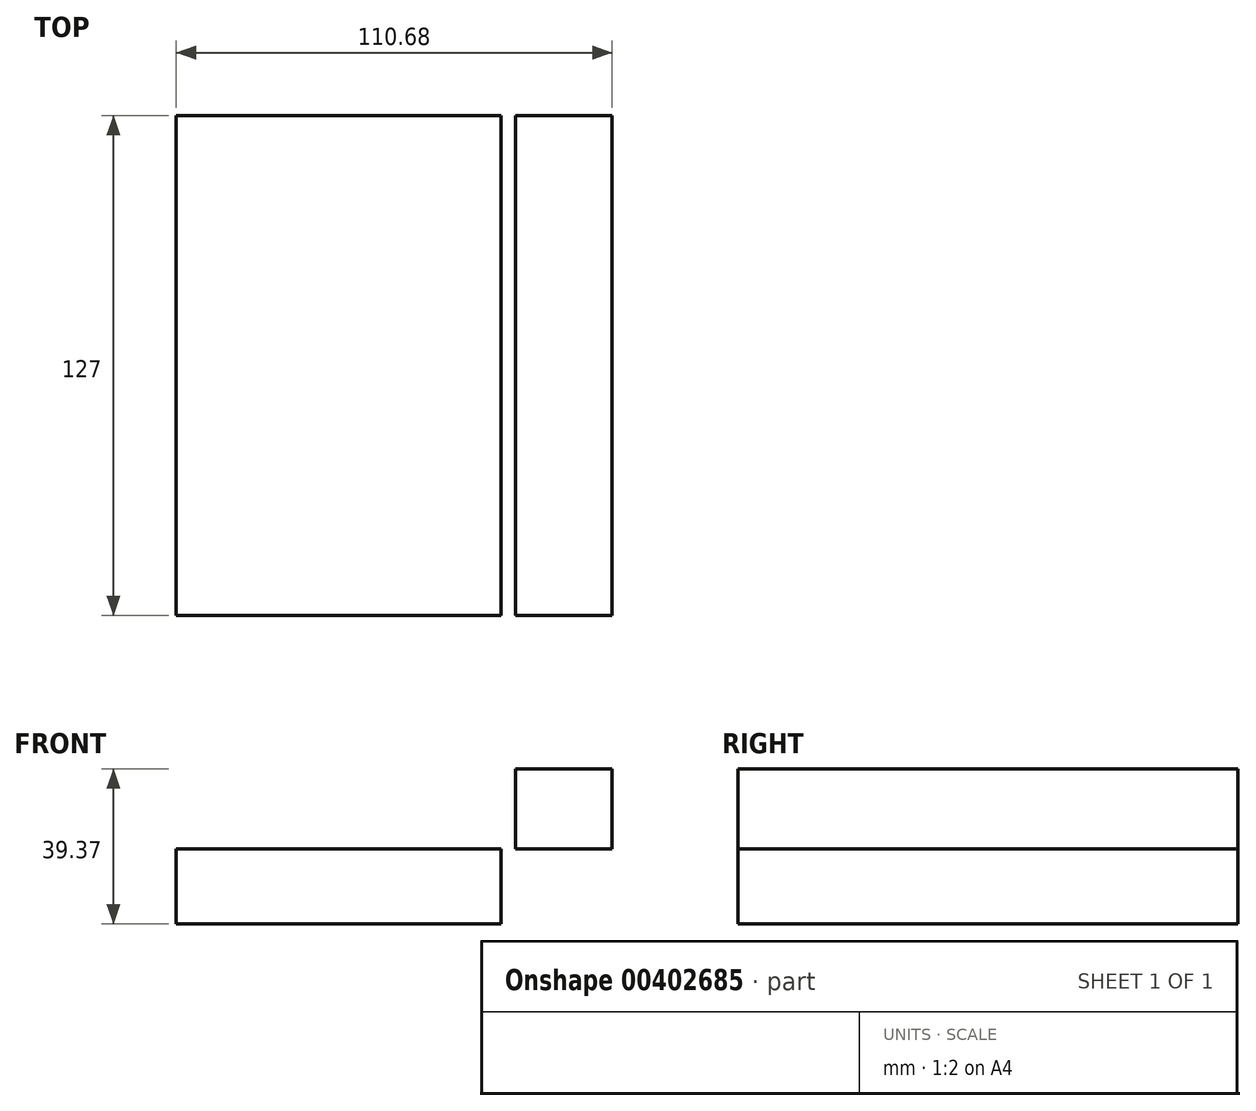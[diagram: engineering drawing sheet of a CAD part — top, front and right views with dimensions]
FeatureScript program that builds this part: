
annotation { "Feature Type Name" : "Feature", "Feature Type Description" : "" }
export const myFeature = defineFeature(function(context is Context, id is Id, definition is map)
    precondition{}
    {
        {
            var Q0;
            Q0=qCreatedBy(makeId("Front.planeOp"),FACE);
            var sketch = newSketch(context, id + "F0", { "sketchPlane" : qUnion([Q0])});
            skLineSegment(sketch, "E0.bottom", {"start": v(-41.28, -9.53) * mm, "end": v(41.28, -9.53) * mm});
            skLineSegment(sketch, "E0.top", {"start": v(-41.28, 9.53) * mm, "end": v(41.28, 9.53) * mm});
            skLineSegment(sketch, "E0.left", {"start": v(-41.28, -9.53) * mm, "end": v(-41.28, 9.53) * mm});
            skLineSegment(sketch, "E0.right", {"start": v(41.28, -9.53) * mm, "end": v(41.28, 9.52) * mm});
            skPoint(sketch, "E0.middle", {"position": v(0, 0) * mm});
            skLineSegment(sketch, "E1.bottom", {"start": v(44.85, 9.53) * mm, "end": v(69.41, 9.53) * mm});
            skLineSegment(sketch, "E1.top", {"start": v(44.85, 29.85) * mm, "end": v(69.41, 29.85) * mm});
            skLineSegment(sketch, "E1.left", {"start": v(44.85, 9.53) * mm, "end": v(44.85, 29.85) * mm});
            skLineSegment(sketch, "E1.right", {"start": v(69.41, 9.53) * mm, "end": v(69.41, 29.85) * mm});
            skPoint(sketch, "E1.middle", {"position": v(57.13, 19.69) * mm});
            skLineSegment(sketch, "E2", {"start": v(41.28, 9.52) * mm, "end": v(41.28, 29) * mm});
            skArc(sketch, "E3", {"start": v(41.28, 29) * mm, "mid": v(42.46, 31.87) * mm, "end": v(45.32, 33.05) * mm});
            skLineSegment(sketch, "E4", {"start": v(45.32, 33.05) * mm, "end": v(51.92, 33.05) * mm});
            skLineSegment(sketch, "E5.0", {"start": v(45.32, 58.45) * mm, "end": v(51.92, 58.45) * mm});
            skArc(sketch, "E5.1", {"start": v(15.88, 29) * mm, "mid": v(24.5, 49.83) * mm, "end": v(45.32, 58.45) * mm});
            skLineSegment(sketch, "E5.2", {"start": v(15.88, 9.52) * mm, "end": v(15.88, 29) * mm});
            skFitSpline(sketch, "E6", {"points": [v(-41.28, 9.53) * mm, v(45.32, 58.45) * mm], "startDerivative": vector(123.83, 28.76) * mm, "endDerivative": vector(242.05, -17.05) * mm});
            skSolve(sketch);
        }
        {
            var Q0;
            Q0=makeQuery(id+"F0.imprint","IMPRINT",FACE,{"disambiguationData":[TD([[makeQuery(id+"F0.imprint","IMPRINT",EDGE,{"derivedFrom":sQuery(id+"F0.wireOp",EDGE,"E0.bottom")}),1.0]])]});
            var Q1;
            Q1=makeQuery(id+"F0.imprint","IMPRINT",FACE,{"disambiguationData":[TD([[makeQuery(id+"F0.imprint","IMPRINT",EDGE,{"derivedFrom":sQuery(id+"F0.wireOp",EDGE,"E5.1")}),1.0]])]});
            var Q2;
            Q2=makeQuery(id+"F0.imprint","IMPRINT",FACE,{"disambiguationData":[TD([[makeQuery(id+"F0.imprint","IMPRINT",EDGE,{"derivedFrom":sQuery(id+"F0.wireOp",EDGE,"E1.bottom")}),1.0]])]});
            extrude(context, id + "F1", {"entities" : qUnion([Q0, Q1, Q2]), "endBound" : BoundingType.SYMMETRIC, "depth" : 127 * mm});
        }
    });
